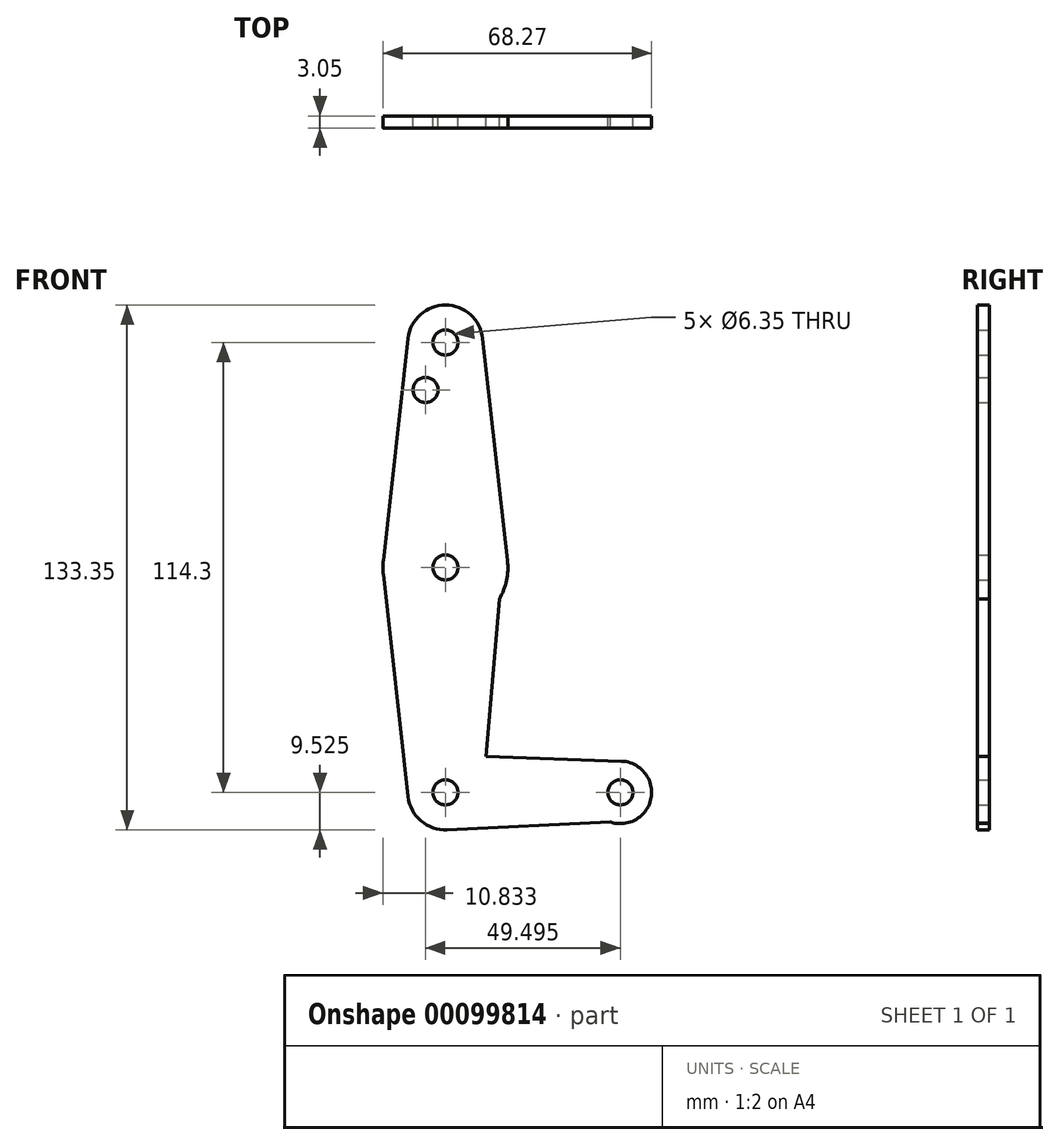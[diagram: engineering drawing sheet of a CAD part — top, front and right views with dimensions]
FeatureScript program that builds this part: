
annotation { "Feature Type Name" : "Feature", "Feature Type Description" : "" }
export const myFeature = defineFeature(function(context is Context, id is Id, definition is map)
    precondition{}
    {
        {
            var Q0;
            Q0=qCreatedBy(makeId("Front.planeOp"),FACE);
            var sketch = newSketch(context, id + "F0", { "sketchPlane" : qUnion([Q0])});
            skLineSegment(sketch, "E0", {"start": v(0.13, 113.82) * mm, "end": v(0.13, -0.48) * mm, "construction": true});
            skLineSegment(sketch, "E1", {"start": v(0.13, -0.48) * mm, "end": v(44.58, -0.48) * mm, "construction": true});
            skCircle(sketch, "E2", {"center": v(0.13, 113.82) * mm, "radius": 9.53 * mm});
            skCircle(sketch, "E3", {"center": v(0.13, -0.48) * mm, "radius": 9.53 * mm});
            skCircle(sketch, "E4", {"center": v(44.58, -0.48) * mm, "radius": 7.94 * mm});
            skCircle(sketch, "E5", {"center": v(0.13, 56.67) * mm, "radius": 15.88 * mm});
            skLineSegment(sketch, "E6", {"start": v(-9.34, 114.87) * mm, "end": v(-15.65, 58.43) * mm});
            skLineSegment(sketch, "E7", {"start": v(9.6, 114.87) * mm, "end": v(15.9, 58.43) * mm});
            skLineSegment(sketch, "E8", {"start": v(-15.65, 54.9) * mm, "end": v(-9.34, -1.54) * mm});
            skLineSegment(sketch, "E9", {"start": v(0.58, -10) * mm, "end": v(42.12, -8.03) * mm});
            skLineSegment(sketch, "E10", {"start": v(13.84, 48.67) * mm, "end": v(9.62, -1.29) * mm});
            skLineSegment(sketch, "E11", {"start": v(0.47, 9.03) * mm, "end": v(44.86, 7.45) * mm});
            skCircle(sketch, "E12", {"center": v(0.13, 113.82) * mm, "radius": 3.18 * mm});
            skCircle(sketch, "E13", {"center": v(-4.92, 101.78) * mm, "radius": 3.18 * mm});
            skCircle(sketch, "E14", {"center": v(0.13, 56.67) * mm, "radius": 3.18 * mm});
            skCircle(sketch, "E15", {"center": v(0.13, -0.48) * mm, "radius": 3.18 * mm});
            skCircle(sketch, "E16", {"center": v(44.58, -0.48) * mm, "radius": 3.18 * mm});
            skSolve(sketch);
        }
        {
            var Q0;
            Q0 = qSketchRegion(id + "F0", true);
            extrude(context, id + "F1", {"entities" : qUnion([Q0]), "depth" : 3.05 * mm});
        }
    });
